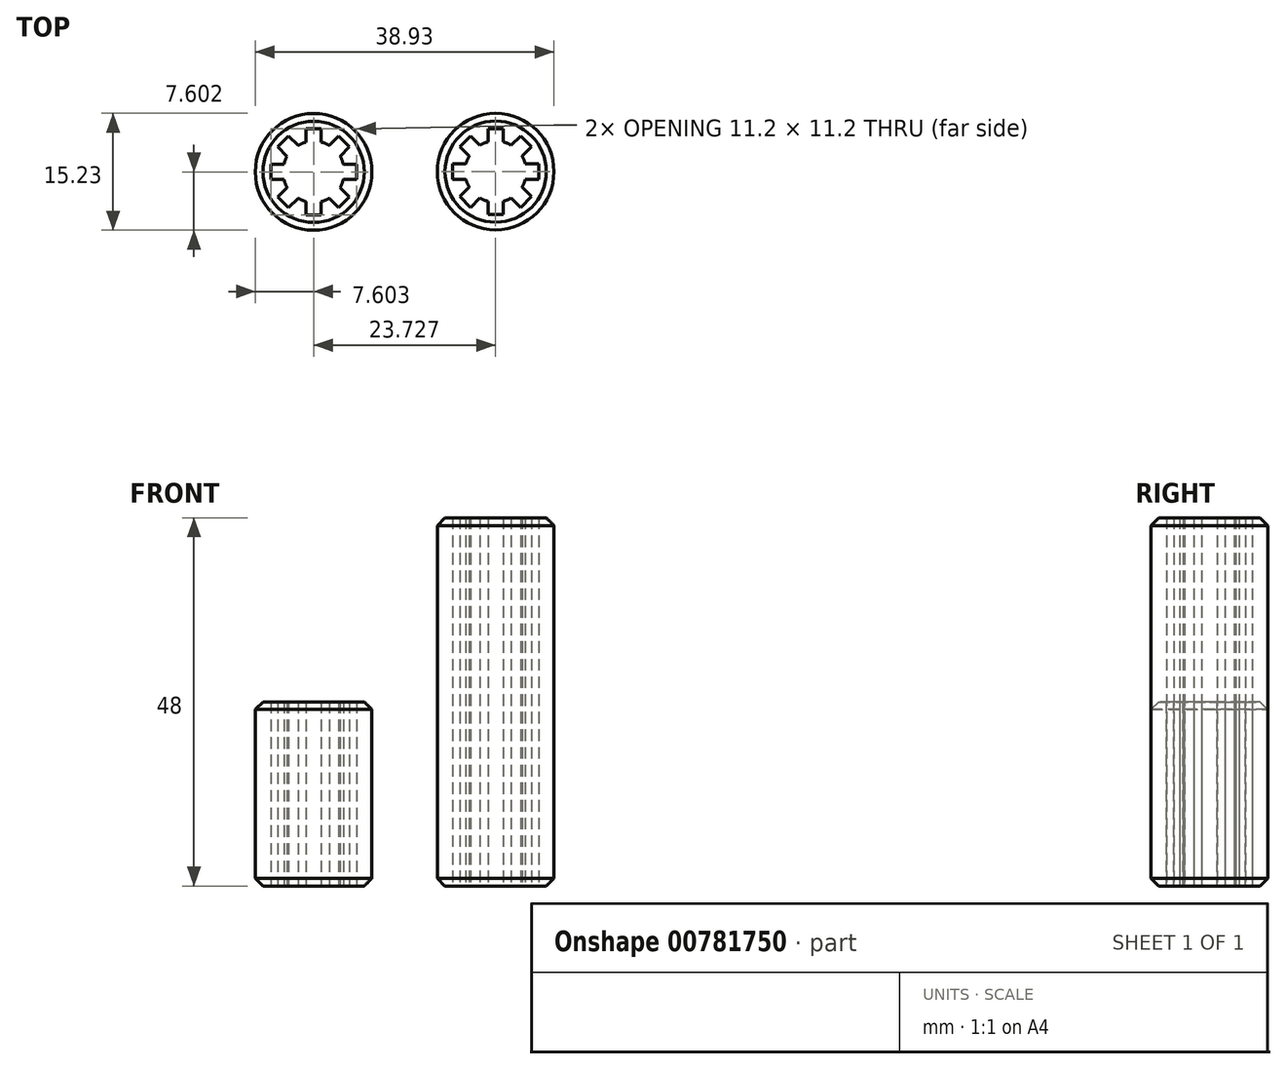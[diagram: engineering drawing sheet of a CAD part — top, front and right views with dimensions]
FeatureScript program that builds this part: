
annotation { "Feature Type Name" : "Feature", "Feature Type Description" : "" }
export const myFeature = defineFeature(function(context is Context, id is Id, definition is map)
    precondition{}
    {
        {
            var Q0;
            Q0=qCreatedBy(makeId("Top.planeOp"),FACE);
            var sketch = newSketch(context, id + "F0", { "sketchPlane" : qUnion([Q0])});
            skCircle(sketch, "E0", {"center": v(0, 0) * mm, "radius": 7.6 * mm});
            skCircle(sketch, "E1", {"center": v(0, 0) * mm, "radius": 4 * mm});
            skLineSegment(sketch, "E2.bottom", {"start": v(-1, 2.88) * mm, "end": v(1, 2.88) * mm});
            skLineSegment(sketch, "E2.top", {"start": v(-1, 5.6) * mm, "end": v(1, 5.6) * mm});
            skLineSegment(sketch, "E2.left", {"start": v(-1, 2.88) * mm, "end": v(-1, 5.6) * mm});
            skLineSegment(sketch, "E2.right", {"start": v(1, 2.88) * mm, "end": v(1, 5.6) * mm});
            skLineSegment(sketch, "E3.1.0", {"start": v(-2.75, 1.33) * mm, "end": v(-4.67, 3.25) * mm});
            skLineSegment(sketch, "E3.1.1", {"start": v(-4.67, 3.25) * mm, "end": v(-3.25, 4.67) * mm});
            skLineSegment(sketch, "E3.1.2", {"start": v(-1.33, 2.75) * mm, "end": v(-3.25, 4.67) * mm});
            skLineSegment(sketch, "E3.1.3", {"start": v(-2.75, 1.33) * mm, "end": v(-1.33, 2.75) * mm});
            skLineSegment(sketch, "E3.2.0", {"start": v(-2.88, -1) * mm, "end": v(-5.6, -1) * mm});
            skLineSegment(sketch, "E3.2.1", {"start": v(-5.6, -1) * mm, "end": v(-5.6, 1) * mm});
            skLineSegment(sketch, "E3.2.2", {"start": v(-2.88, 1) * mm, "end": v(-5.6, 1) * mm});
            skLineSegment(sketch, "E3.2.3", {"start": v(-2.88, -1) * mm, "end": v(-2.88, 1) * mm});
            skLineSegment(sketch, "E4.1.3.0", {"start": v(-1.33, -2.75) * mm, "end": v(-3.25, -4.67) * mm});
            skLineSegment(sketch, "E4.3.3.0", {"start": v(-3.25, -4.67) * mm, "end": v(-4.67, -3.25) * mm});
            skLineSegment(sketch, "E4.6.3.0", {"start": v(-2.75, -1.33) * mm, "end": v(-4.67, -3.25) * mm});
            skLineSegment(sketch, "E4.9.3.0", {"start": v(-1.33, -2.75) * mm, "end": v(-2.75, -1.33) * mm});
            skLineSegment(sketch, "E4.1.4.0", {"start": v(1, -2.88) * mm, "end": v(1, -5.6) * mm});
            skLineSegment(sketch, "E4.3.4.0", {"start": v(1, -5.6) * mm, "end": v(-1, -5.6) * mm});
            skLineSegment(sketch, "E4.6.4.0", {"start": v(-1, -2.88) * mm, "end": v(-1, -5.6) * mm});
            skLineSegment(sketch, "E4.9.4.0", {"start": v(1, -2.88) * mm, "end": v(-1, -2.88) * mm});
            skLineSegment(sketch, "E4.1.5.0", {"start": v(2.75, -1.33) * mm, "end": v(4.67, -3.25) * mm});
            skLineSegment(sketch, "E4.3.5.0", {"start": v(4.67, -3.25) * mm, "end": v(3.25, -4.67) * mm});
            skLineSegment(sketch, "E4.6.5.0", {"start": v(1.33, -2.75) * mm, "end": v(3.25, -4.67) * mm});
            skLineSegment(sketch, "E4.9.5.0", {"start": v(2.75, -1.33) * mm, "end": v(1.33, -2.75) * mm});
            skLineSegment(sketch, "E4.1.6.0", {"start": v(2.88, 1) * mm, "end": v(5.6, 1) * mm});
            skLineSegment(sketch, "E4.3.6.0", {"start": v(5.6, 1) * mm, "end": v(5.6, -1) * mm});
            skLineSegment(sketch, "E4.6.6.0", {"start": v(2.88, -1) * mm, "end": v(5.6, -1) * mm});
            skLineSegment(sketch, "E4.9.6.0", {"start": v(2.88, 1) * mm, "end": v(2.88, -1) * mm});
            skLineSegment(sketch, "E4.1.7.0", {"start": v(1.33, 2.75) * mm, "end": v(3.25, 4.67) * mm});
            skLineSegment(sketch, "E4.3.7.0", {"start": v(3.25, 4.67) * mm, "end": v(4.67, 3.25) * mm});
            skLineSegment(sketch, "E4.6.7.0", {"start": v(2.75, 1.33) * mm, "end": v(4.67, 3.25) * mm});
            skLineSegment(sketch, "E4.9.7.0", {"start": v(1.33, 2.75) * mm, "end": v(2.75, 1.33) * mm});
            skCircle(sketch, "E5", {"center": v(-23.73, -0.03) * mm, "radius": 7.6 * mm});
            skCircle(sketch, "E6", {"center": v(-23.73, -0.03) * mm, "radius": 4 * mm});
            skLineSegment(sketch, "E7.bottom", {"start": v(-24.73, 2.86) * mm, "end": v(-22.73, 2.86) * mm});
            skLineSegment(sketch, "E7.top", {"start": v(-24.73, 5.57) * mm, "end": v(-22.73, 5.57) * mm});
            skLineSegment(sketch, "E7.left", {"start": v(-24.73, 2.86) * mm, "end": v(-24.73, 5.57) * mm});
            skLineSegment(sketch, "E7.right", {"start": v(-22.73, 2.86) * mm, "end": v(-22.73, 5.57) * mm});
            skLineSegment(sketch, "E8.1.0", {"start": v(-26.47, 1.3) * mm, "end": v(-28.4, 3.22) * mm});
            skLineSegment(sketch, "E8.1.1", {"start": v(-28.4, 3.22) * mm, "end": v(-26.98, 4.64) * mm});
            skLineSegment(sketch, "E8.1.2", {"start": v(-25.06, 2.72) * mm, "end": v(-26.98, 4.64) * mm});
            skLineSegment(sketch, "E8.1.3", {"start": v(-26.47, 1.3) * mm, "end": v(-25.06, 2.72) * mm});
            skLineSegment(sketch, "E8.2.0", {"start": v(-26.61, -1.03) * mm, "end": v(-29.33, -1.03) * mm});
            skLineSegment(sketch, "E8.2.1", {"start": v(-29.33, -1.03) * mm, "end": v(-29.33, 0.97) * mm});
            skLineSegment(sketch, "E8.2.2", {"start": v(-26.61, 0.97) * mm, "end": v(-29.33, 0.97) * mm});
            skLineSegment(sketch, "E8.2.3", {"start": v(-26.61, -1.03) * mm, "end": v(-26.61, 0.97) * mm});
            skLineSegment(sketch, "E9.1.3.0", {"start": v(-25.06, -2.77) * mm, "end": v(-26.98, -4.7) * mm});
            skLineSegment(sketch, "E9.3.3.0", {"start": v(-26.98, -4.7) * mm, "end": v(-28.4, -3.28) * mm});
            skLineSegment(sketch, "E9.6.3.0", {"start": v(-26.47, -1.36) * mm, "end": v(-28.4, -3.28) * mm});
            skLineSegment(sketch, "E9.9.3.0", {"start": v(-25.06, -2.77) * mm, "end": v(-26.47, -1.36) * mm});
            skLineSegment(sketch, "E9.1.4.0", {"start": v(-22.73, -2.91) * mm, "end": v(-22.73, -5.63) * mm});
            skLineSegment(sketch, "E9.3.4.0", {"start": v(-22.73, -5.63) * mm, "end": v(-24.73, -5.63) * mm});
            skLineSegment(sketch, "E9.6.4.0", {"start": v(-24.73, -2.91) * mm, "end": v(-24.73, -5.63) * mm});
            skLineSegment(sketch, "E9.9.4.0", {"start": v(-22.73, -2.91) * mm, "end": v(-24.73, -2.91) * mm});
            skLineSegment(sketch, "E9.1.5.0", {"start": v(-20.98, -1.36) * mm, "end": v(-19.06, -3.28) * mm});
            skLineSegment(sketch, "E9.3.5.0", {"start": v(-19.06, -3.28) * mm, "end": v(-20.47, -4.7) * mm});
            skLineSegment(sketch, "E9.6.5.0", {"start": v(-22.4, -2.77) * mm, "end": v(-20.47, -4.7) * mm});
            skLineSegment(sketch, "E9.9.5.0", {"start": v(-20.98, -1.36) * mm, "end": v(-22.4, -2.77) * mm});
            skLineSegment(sketch, "E9.1.6.0", {"start": v(-20.84, 0.97) * mm, "end": v(-18.13, 0.97) * mm});
            skLineSegment(sketch, "E9.3.6.0", {"start": v(-18.13, 0.97) * mm, "end": v(-18.13, -1.03) * mm});
            skLineSegment(sketch, "E9.6.6.0", {"start": v(-20.84, -1.03) * mm, "end": v(-18.13, -1.03) * mm});
            skLineSegment(sketch, "E9.9.6.0", {"start": v(-20.84, 0.97) * mm, "end": v(-20.84, -1.03) * mm});
            skLineSegment(sketch, "E9.1.7.0", {"start": v(-22.4, 2.72) * mm, "end": v(-20.47, 4.64) * mm});
            skLineSegment(sketch, "E9.3.7.0", {"start": v(-20.47, 4.64) * mm, "end": v(-19.06, 3.22) * mm});
            skLineSegment(sketch, "E9.6.7.0", {"start": v(-20.98, 1.3) * mm, "end": v(-19.06, 3.22) * mm});
            skLineSegment(sketch, "E9.9.7.0", {"start": v(-22.4, 2.72) * mm, "end": v(-20.98, 1.3) * mm});
            skSolve(sketch);
        }
        {
            var Q0;
            Q0=makeQuery(id+"F0.imprint","IMPRINT",FACE,{"disambiguationData":[TD([[makeQuery(id+"F0.imprint","IMPRINT",EDGE,{"derivedFrom":sQuery(id+"F0.wireOp",EDGE,"E0")}),1.0]])]});
            extrude(context, id + "F1", {"entities" : qUnion([Q0]), "depth" : 48 * mm, "offsetDistance" : 25 * mm});
        }
        {
            var Q0;
            Q0=makeQuery(id+"F0.imprint","IMPRINT",FACE,{"disambiguationData":[TD([[makeQuery(id+"F0.imprint","IMPRINT",EDGE,{"derivedFrom":sQuery(id+"F0.wireOp",EDGE,"E5")}),1.0]])]});
            extrude(context, id + "F2", {"entities" : qUnion([Q0]), "depth" : 24 * mm, "offsetDistance" : 25 * mm});
        }
        {
            var Q0;
            Q0=makeQuery(id+"F1.opExtrude","CAP_EDGE",EDGE,{"disambiguationData":[OSD([sQuery(id+"F0.wireOp",EDGE,"E0")])],"isStart":false});
            var Q1;
            Q1=makeQuery(id+"F1.opExtrude","CAP_EDGE",EDGE,{"disambiguationData":[OSD([sQuery(id+"F0.wireOp",EDGE,"E0")])],"isStart":true});
            var Q2;
            Q2=makeQuery(id+"F2.opExtrude","CAP_EDGE",EDGE,{"disambiguationData":[OSD([sQuery(id+"F0.wireOp",EDGE,"E5")])],"isStart":false});
            var Q3;
            Q3=makeQuery(id+"F2.opExtrude","CAP_EDGE",EDGE,{"disambiguationData":[OSD([sQuery(id+"F0.wireOp",EDGE,"E5")])],"isStart":true});
            chamfer(context, id + "F3", {"entities" : qUnion([Q0, Q1, Q2, Q3]), "width" : 1 * mm, "tangentPropagation" : true});
        }
    });
